# Revit family: TD92_ANN033_TRA011_RVT20_R00
name_source: partatom
category: Mobiliário
units: mm (PartAtom-declared; Revit-internal decimal feet)

## family parameters
Com base no plano de trabalho = Não
Compartilhado = Não
Corte com vazios quando carregada = Não
Número OmniClass = 23.40.20.00
Ponto de cálculo do ambiente = Não
Sempre na vertical = Sim
Título OmniClass = General Furniture and Specialties

## types (1)
- TD92_ANN033_TRA011_RVT20_R00
    Descrição = O que a gente precisa em nossa casa ou escritório são itens bonitos, que unem elegância, modernidade e que sejam extremamente práticos. A Cadeira Tramontina Anna é ideal para você. Produzida em policarbonato, que é 250 vezes mais resistente que o vidro, além de ser 50% mais leve, ela resiste à carga estática de até 182 Kg. Seu design torna-se diferenciado para agregar modernidade e sofisticação ao seu ambiente interno.
    Elevação padrão = 0  [stored 0 ft]
    Fabricante = Tramontina Delta S/A
    Modelo = Cadeira Tramontina Anna em Policarbonato Transparente
    Nota-chave = 92033011
    URL = https://www.tramontinastore.com

note: [stored X ft] marks values corroborated as IEEE doubles in the binary element streams (Revit-internal decimal feet)
